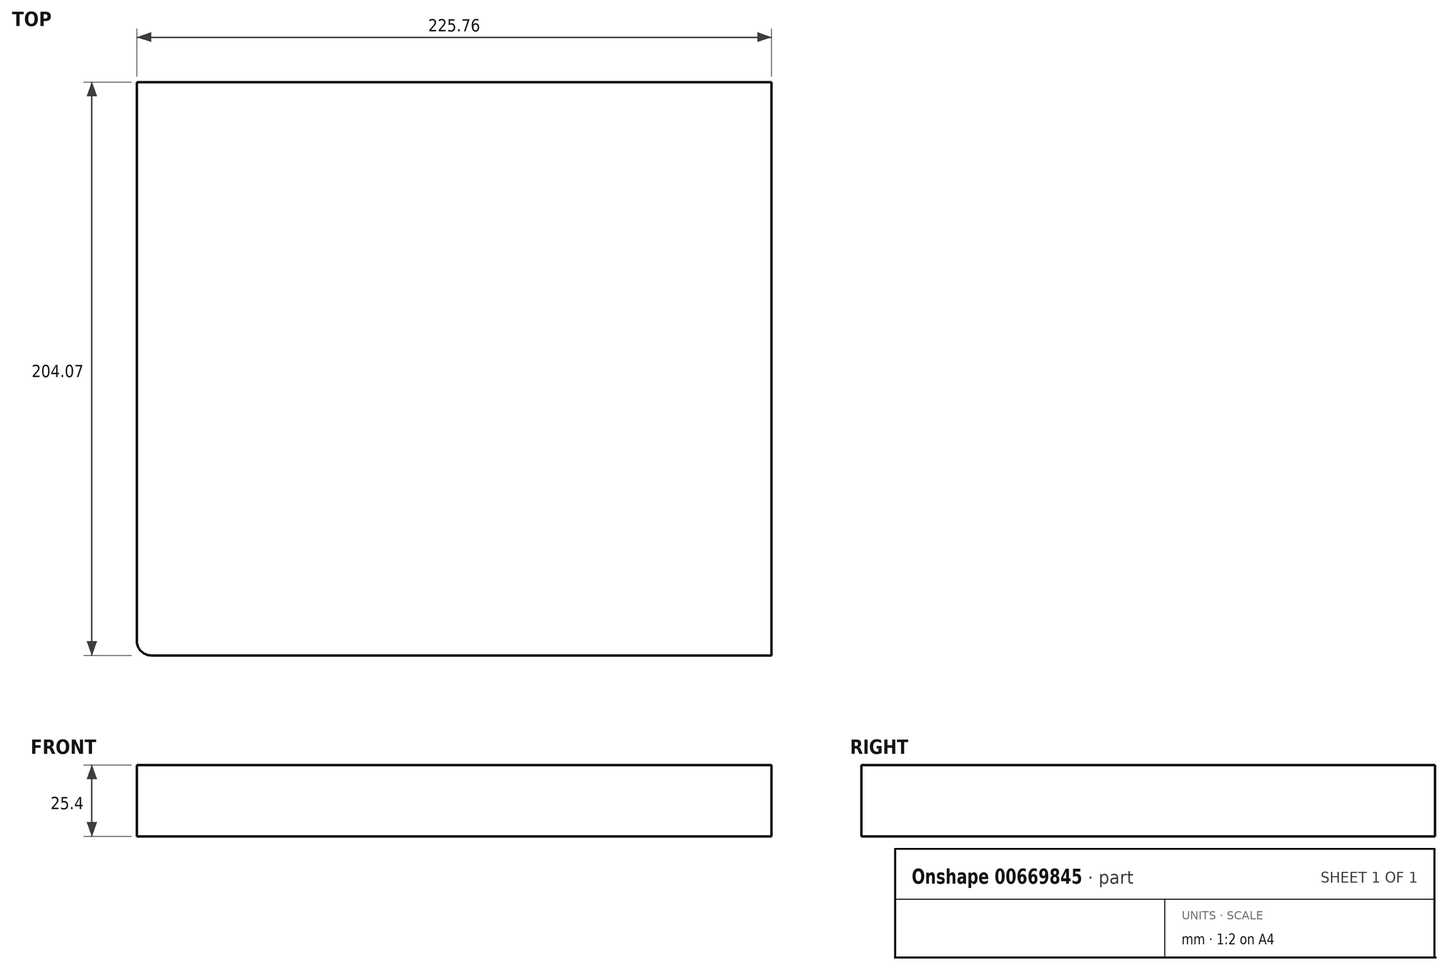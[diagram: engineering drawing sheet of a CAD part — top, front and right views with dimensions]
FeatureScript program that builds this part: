
annotation { "Feature Type Name" : "Feature", "Feature Type Description" : "" }
export const myFeature = defineFeature(function(context is Context, id is Id, definition is map)
    precondition{}
    {
        {
            var Q0;
            Q0=qCreatedBy(makeId("Top.planeOp"),FACE);
            var sketch = newSketch(context, id + "F0", { "sketchPlane" : qUnion([Q0])});
            skLineSegment(sketch, "E0.bottom", {"start": v(-49.45, 68.54) * mm, "end": v(-61.8, 68.54) * mm});
            skLineSegment(sketch, "E0.top", {"start": v(-49.45, 104.46) * mm, "end": v(-61.8, 104.46) * mm});
            skLineSegment(sketch, "E0.left", {"start": v(-49.45, 68.54) * mm, "end": v(-49.45, 104.46) * mm});
            skLineSegment(sketch, "E0.right", {"start": v(-61.8, 68.54) * mm, "end": v(-61.8, 104.46) * mm});
            skPoint(sketch, "E0.middle", {"position": v(-55.63, 86.5) * mm});
            skLineSegment(sketch, "E1.bottom", {"start": v(-49.45, 68.54) * mm, "end": v(176.31, 68.54) * mm});
            skLineSegment(sketch, "E1.top", {"start": v(-49.45, -135.53) * mm, "end": v(176.31, -135.53) * mm});
            skLineSegment(sketch, "E1.left", {"start": v(-49.45, 68.54) * mm, "end": v(-49.45, -135.53) * mm});
            skLineSegment(sketch, "E1.right", {"start": v(176.31, 68.54) * mm, "end": v(176.31, -135.53) * mm});
            skPoint(sketch, "E1.middle", {"position": v(63.43, -33.5) * mm});
            skSolve(sketch);
        }
        {
            var Q0;
            Q0=makeQuery(id+"F0.imprint","IMPRINT",FACE,{"disambiguationData":[TD([[makeQuery(id+"F0.imprint","IMPRINT",EDGE,{"derivedFrom":sQuery(id+"F0.wireOp",EDGE,"E1.bottom")}),-1.0]])]});
            extrude(context, id + "F1", {"entities" : qUnion([Q0]), "depth" : 25.4 * mm, "offsetDistance" : 25.4 * mm});
        }
        {
            var Q0;
            Q0=makeQuery(id+"F1.opExtrude","SWEPT_EDGE",EDGE,{"disambiguationData":[OSD([sQuery(id+"F0.wireOp",EDGE,"E1.top"),sQuery(id+"F0.wireOp",EDGE,"E1.left")])]});
            fillet(context, id + "F2", {"entities" : qUnion([Q0]), "radius" : 5.08 * mm, "tangentPropagation" : true, "allowEdgeOverflow" : false});
        }
    });
